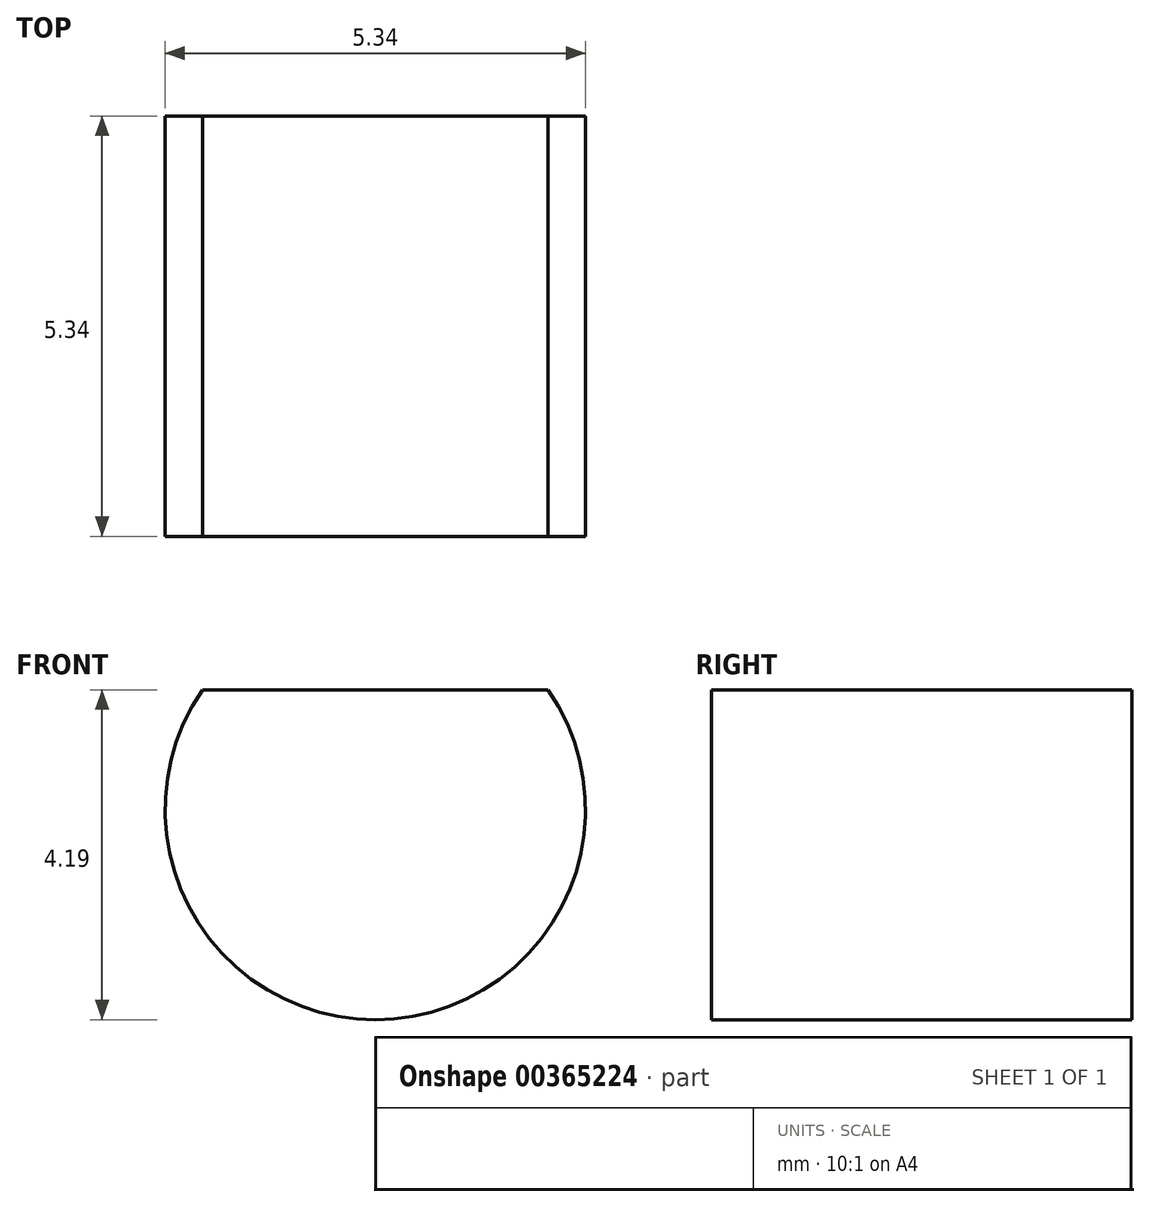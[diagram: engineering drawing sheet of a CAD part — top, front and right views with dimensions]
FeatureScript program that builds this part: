
annotation { "Feature Type Name" : "Feature", "Feature Type Description" : "" }
export const myFeature = defineFeature(function(context is Context, id is Id, definition is map)
    precondition{}
    {
        {
            var Q0;
            Q0=qCreatedBy(makeId("Front.planeOp"),FACE);
            var sketch = newSketch(context, id + "F0", { "sketchPlane" : qUnion([Q0])});
            skArc(sketch, "E0", {"start": v(-2.2, 1.52) * mm, "mid": v(0, -2.67) * mm, "end": v(2.2, 1.52) * mm});
            skLineSegment(sketch, "E1", {"start": v(-2.2, 1.52) * mm, "end": v(2.2, 1.52) * mm});
            skSolve(sketch);
        }
        {
            var Q0;
            Q0 = qSketchRegion(id + "F0", true);
            extrude(context, id + "F1", {"entities" : qUnion([Q0]), "depth" : 5.34 * mm});
        }
    });
